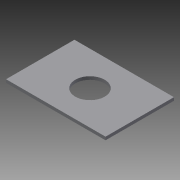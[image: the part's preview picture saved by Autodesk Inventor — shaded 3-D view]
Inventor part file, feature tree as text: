
AUTODESK INVENTOR PART (.ipt)
format: ipt  version: 2013 (Build 170138000, 138)  size: 82,432 bytes
history: native  units: in
note: dims shown in document units (in); Inventor stores cm internally (conversion verified against a paired STEP export)
features: extrude x2, sketch x2
ambient origin geometry x8: Origin, YZ Plane, XZ Plane, XY Plane, X Axis, Y Axis, Z Axis, Center Point
bodies: Solid1 (feature_tree)
feature tree (4):
  extrude  "Extrusion1"  Depth=4.0in
  extrude  "Extrusion2"  Depth=1.1811in
  sketch  "Sketch1"  dims[d4=0.125in d5=0.0in d6=4.0in]
  sketch  "Sketch2"  dims[d7=2.75in d8=1.1811in d9=2.0in d10=2.0in d11=1.375in d12=1.375in d13=0.125in d14=0.0in]
